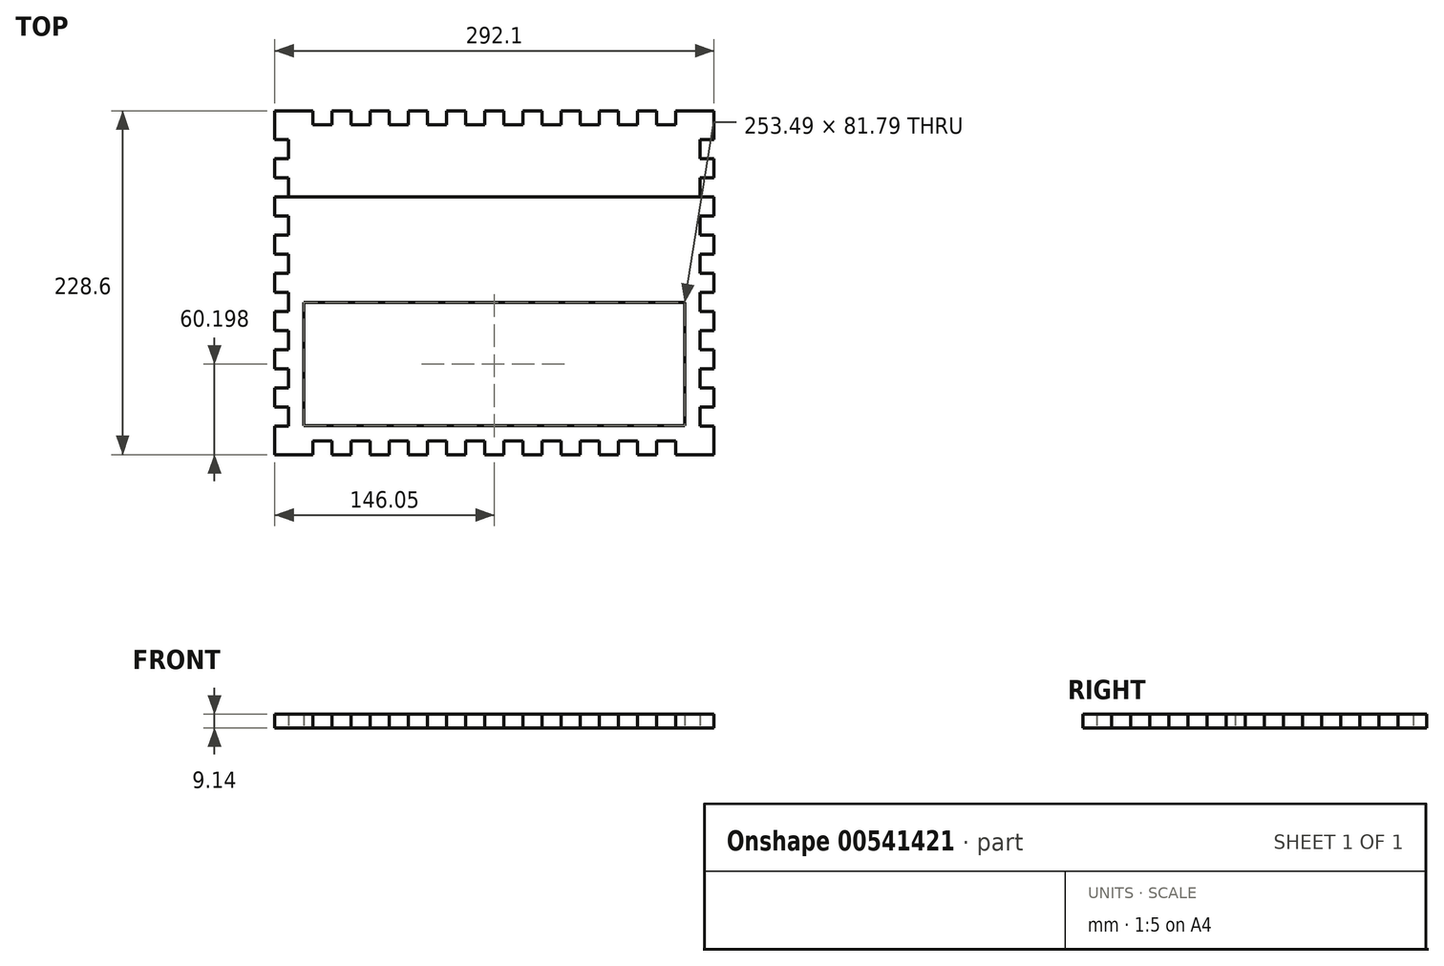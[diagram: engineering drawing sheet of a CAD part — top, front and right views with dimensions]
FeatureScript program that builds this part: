
annotation { "Feature Type Name" : "Feature", "Feature Type Description" : "" }
export const myFeature = defineFeature(function(context is Context, id is Id, definition is map)
    precondition{}
    {
        {
            var Q0;
            Q0=qCreatedBy(makeId("Top.planeOp"),FACE);
            var sketch = newSketch(context, id + "F0", { "sketchPlane" : qUnion([Q0])});
            skLineSegment(sketch, "E0.bottom", {"start": v(0, 0) * mm, "end": v(25.4, 0) * mm});
            skLineSegment(sketch, "E0.left", {"start": v(0, 0) * mm, "end": v(0, -19.05) * mm});
            skLineSegment(sketch, "E1", {"start": v(25.4, 0) * mm, "end": v(25.4, -9.14) * mm});
            skLineSegment(sketch, "E2", {"start": v(25.4, -9.14) * mm, "end": v(38.1, -9.14) * mm});
            skLineSegment(sketch, "E3", {"start": v(38.1, -9.14) * mm, "end": v(38.1, 0) * mm});
            skLineSegment(sketch, "E4", {"start": v(38.1, 0) * mm, "end": v(50.8, 0) * mm});
            skLineSegment(sketch, "E5", {"start": v(50.8, 0) * mm, "end": v(50.8, -9.14) * mm});
            skLineSegment(sketch, "E6", {"start": v(50.8, -9.14) * mm, "end": v(63.5, -9.14) * mm});
            skLineSegment(sketch, "E7", {"start": v(63.5, -9.14) * mm, "end": v(63.5, 0) * mm});
            skLineSegment(sketch, "E8", {"start": v(63.5, 0) * mm, "end": v(76.2, 0) * mm});
            skLineSegment(sketch, "E9", {"start": v(76.2, 0) * mm, "end": v(76.2, -9.14) * mm});
            skLineSegment(sketch, "E10", {"start": v(76.2, -9.14) * mm, "end": v(88.9, -9.14) * mm});
            skLineSegment(sketch, "E11", {"start": v(88.9, -9.14) * mm, "end": v(88.9, 0) * mm});
            skLineSegment(sketch, "E12", {"start": v(88.9, 0) * mm, "end": v(101.6, 0) * mm});
            skLineSegment(sketch, "E13", {"start": v(101.6, 0) * mm, "end": v(101.6, -9.14) * mm});
            skLineSegment(sketch, "E14", {"start": v(101.6, -9.14) * mm, "end": v(114.3, -9.14) * mm});
            skLineSegment(sketch, "E15", {"start": v(114.3, -9.14) * mm, "end": v(114.3, 0) * mm});
            skLineSegment(sketch, "E16", {"start": v(114.3, 0) * mm, "end": v(127, 0) * mm});
            skLineSegment(sketch, "E17", {"start": v(127, 0) * mm, "end": v(127, -9.14) * mm});
            skLineSegment(sketch, "E18", {"start": v(127, -9.14) * mm, "end": v(139.7, -9.14) * mm});
            skLineSegment(sketch, "E19", {"start": v(139.7, -9.14) * mm, "end": v(139.7, 0) * mm});
            skLineSegment(sketch, "E20.trimOffspring", {"start": v(139.7, 0) * mm, "end": v(152.4, 0) * mm});
            skLineSegment(sketch, "E21", {"start": v(152.4, 0) * mm, "end": v(152.4, -9.14) * mm});
            skLineSegment(sketch, "E22", {"start": v(152.4, -9.14) * mm, "end": v(165.1, -9.14) * mm});
            skLineSegment(sketch, "E23", {"start": v(165.1, -9.14) * mm, "end": v(165.1, 0) * mm});
            skLineSegment(sketch, "E24", {"start": v(165.1, 0) * mm, "end": v(177.8, 0) * mm});
            skLineSegment(sketch, "E25", {"start": v(177.8, 0) * mm, "end": v(177.8, -9.14) * mm});
            skLineSegment(sketch, "E26", {"start": v(177.8, -9.14) * mm, "end": v(190.5, -9.14) * mm});
            skLineSegment(sketch, "E27", {"start": v(190.5, -9.14) * mm, "end": v(190.5, 0) * mm});
            skLineSegment(sketch, "E28", {"start": v(190.5, 0) * mm, "end": v(203.2, 0) * mm});
            skLineSegment(sketch, "E29", {"start": v(203.2, 0) * mm, "end": v(203.2, -9.14) * mm});
            skLineSegment(sketch, "E30", {"start": v(203.2, -9.14) * mm, "end": v(215.9, -9.14) * mm});
            skLineSegment(sketch, "E31", {"start": v(215.9, -9.14) * mm, "end": v(215.9, 0) * mm});
            skLineSegment(sketch, "E32.trimOffspring", {"start": v(215.9, 0) * mm, "end": v(228.6, 0) * mm});
            skLineSegment(sketch, "E33", {"start": v(228.6, 0) * mm, "end": v(228.6, -9.14) * mm});
            skLineSegment(sketch, "E34", {"start": v(228.6, -9.14) * mm, "end": v(241.3, -9.14) * mm});
            skLineSegment(sketch, "E35", {"start": v(241.3, -9.14) * mm, "end": v(241.3, 0) * mm});
            skLineSegment(sketch, "E36", {"start": v(241.3, 0) * mm, "end": v(254, 0) * mm});
            skLineSegment(sketch, "E37", {"start": v(254, 0) * mm, "end": v(254, -9.14) * mm});
            skLineSegment(sketch, "E38", {"start": v(254, -9.14) * mm, "end": v(266.7, -9.14) * mm});
            skLineSegment(sketch, "E39", {"start": v(266.7, -9.14) * mm, "end": v(266.7, 0) * mm});
            skLineSegment(sketch, "E40.trimOffspring", {"start": v(266.7, 0) * mm, "end": v(292.1, 0) * mm});
            skLineSegment(sketch, "E41", {"start": v(0, -19.05) * mm, "end": v(9.14, -19.05) * mm});
            skLineSegment(sketch, "E42", {"start": v(9.14, -19.05) * mm, "end": v(9.14, -31.75) * mm});
            skLineSegment(sketch, "E43", {"start": v(9.14, -31.75) * mm, "end": v(0, -31.75) * mm});
            skLineSegment(sketch, "E44", {"start": v(0, -31.75) * mm, "end": v(0, -44.45) * mm});
            skLineSegment(sketch, "E45", {"start": v(0, -44.45) * mm, "end": v(9.14, -44.45) * mm});
            skLineSegment(sketch, "E46", {"start": v(9.14, -44.45) * mm, "end": v(9.14, -57.15) * mm});
            skLineSegment(sketch, "E47", {"start": v(9.14, -57.15) * mm, "end": v(0, -57.15) * mm});
            skLineSegment(sketch, "E48", {"start": v(0, -57.15) * mm, "end": v(0, -69.85) * mm});
            skLineSegment(sketch, "E49", {"start": v(0, -69.85) * mm, "end": v(9.14, -69.85) * mm});
            skLineSegment(sketch, "E50", {"start": v(9.14, -69.85) * mm, "end": v(9.14, -82.55) * mm});
            skLineSegment(sketch, "E51", {"start": v(9.14, -82.55) * mm, "end": v(0, -82.55) * mm});
            skLineSegment(sketch, "E52.trimOffspring", {"start": v(0, -82.55) * mm, "end": v(0, -95.25) * mm});
            skLineSegment(sketch, "E53", {"start": v(0, -95.25) * mm, "end": v(9.14, -95.25) * mm});
            skLineSegment(sketch, "E54", {"start": v(9.14, -95.25) * mm, "end": v(9.14, -107.95) * mm});
            skLineSegment(sketch, "E55", {"start": v(9.14, -107.95) * mm, "end": v(0, -107.95) * mm});
            skLineSegment(sketch, "E56", {"start": v(0, -107.95) * mm, "end": v(0, -120.65) * mm});
            skLineSegment(sketch, "E57", {"start": v(0, -120.65) * mm, "end": v(9.14, -120.65) * mm});
            skLineSegment(sketch, "E58", {"start": v(9.14, -120.65) * mm, "end": v(9.14, -133.35) * mm});
            skLineSegment(sketch, "E59", {"start": v(9.14, -133.35) * mm, "end": v(0, -133.35) * mm});
            skLineSegment(sketch, "E60", {"start": v(0, -133.35) * mm, "end": v(0, -146.05) * mm});
            skLineSegment(sketch, "E61", {"start": v(0, -146.05) * mm, "end": v(9.14, -146.05) * mm});
            skLineSegment(sketch, "E62", {"start": v(9.14, -146.05) * mm, "end": v(9.14, -158.75) * mm});
            skLineSegment(sketch, "E63", {"start": v(9.14, -158.75) * mm, "end": v(0, -158.75) * mm});
            skLineSegment(sketch, "E64.trimOffspring", {"start": v(0, -158.75) * mm, "end": v(0, -171.45) * mm});
            skLineSegment(sketch, "E65", {"start": v(0, -171.45) * mm, "end": v(9.14, -171.45) * mm});
            skLineSegment(sketch, "E66", {"start": v(9.14, -171.45) * mm, "end": v(9.14, -184.15) * mm});
            skLineSegment(sketch, "E67", {"start": v(9.14, -184.15) * mm, "end": v(0, -184.15) * mm});
            skLineSegment(sketch, "E68", {"start": v(0, -184.15) * mm, "end": v(0, -196.85) * mm});
            skLineSegment(sketch, "E69", {"start": v(0, -196.85) * mm, "end": v(9.14, -196.85) * mm});
            skLineSegment(sketch, "E70", {"start": v(9.14, -196.85) * mm, "end": v(9.14, -209.55) * mm});
            skLineSegment(sketch, "E71", {"start": v(9.14, -209.55) * mm, "end": v(0, -209.55) * mm});
            skLineSegment(sketch, "E72", {"start": v(0, -209.55) * mm, "end": v(0, -228.6) * mm});
            skLineSegment(sketch, "E73", {"start": v(146.05, 0) * mm, "end": v(146.05, -55.4) * mm, "construction": true});
            skLineSegment(sketch, "E74", {"start": v(0, -114.3) * mm, "end": v(76.06, -114.3) * mm, "construction": true});
            skLineSegment(sketch, "E75.MirrorCS", {"start": v(292.1, 0) * mm, "end": v(292.1, -19.05) * mm});
            skLineSegment(sketch, "E76.MirrorCS", {"start": v(292.1, -19.05) * mm, "end": v(282.96, -19.05) * mm});
            skLineSegment(sketch, "E77.MirrorCS", {"start": v(282.96, -19.05) * mm, "end": v(282.96, -31.75) * mm});
            skLineSegment(sketch, "E78.MirrorCS", {"start": v(282.96, -31.75) * mm, "end": v(292.1, -31.75) * mm});
            skLineSegment(sketch, "E79.MirrorCS", {"start": v(292.1, -31.75) * mm, "end": v(292.1, -44.45) * mm});
            skLineSegment(sketch, "E80.MirrorCS", {"start": v(292.1, -44.45) * mm, "end": v(282.96, -44.45) * mm});
            skLineSegment(sketch, "E81.MirrorCS", {"start": v(282.96, -44.45) * mm, "end": v(282.96, -57.15) * mm});
            skLineSegment(sketch, "E82.MirrorCS", {"start": v(282.96, -57.15) * mm, "end": v(292.1, -57.15) * mm});
            skLineSegment(sketch, "E83.MirrorCS", {"start": v(292.1, -57.15) * mm, "end": v(292.1, -69.85) * mm});
            skLineSegment(sketch, "E84.MirrorCS", {"start": v(292.1, -69.85) * mm, "end": v(282.96, -69.85) * mm});
            skLineSegment(sketch, "E85.MirrorCS", {"start": v(282.96, -69.85) * mm, "end": v(282.96, -82.55) * mm});
            skLineSegment(sketch, "E86.MirrorCS", {"start": v(282.96, -82.55) * mm, "end": v(292.1, -82.55) * mm});
            skLineSegment(sketch, "E87.MirrorCS", {"start": v(292.1, -82.55) * mm, "end": v(292.1, -95.25) * mm});
            skLineSegment(sketch, "E88.MirrorCS", {"start": v(292.1, -95.25) * mm, "end": v(282.96, -95.25) * mm});
            skLineSegment(sketch, "E89.MirrorCS", {"start": v(282.96, -95.25) * mm, "end": v(282.96, -107.95) * mm});
            skLineSegment(sketch, "E90.MirrorCS", {"start": v(282.96, -107.95) * mm, "end": v(292.1, -107.95) * mm});
            skLineSegment(sketch, "E91.MirrorCS", {"start": v(292.1, -107.95) * mm, "end": v(292.1, -120.65) * mm});
            skLineSegment(sketch, "E92.MirrorCS", {"start": v(292.1, -120.65) * mm, "end": v(282.96, -120.65) * mm});
            skLineSegment(sketch, "E93.MirrorCS", {"start": v(282.96, -120.65) * mm, "end": v(282.96, -133.35) * mm});
            skLineSegment(sketch, "E94.MirrorCS", {"start": v(282.96, -133.35) * mm, "end": v(292.1, -133.35) * mm});
            skLineSegment(sketch, "E95.MirrorCS", {"start": v(292.1, -133.35) * mm, "end": v(292.1, -146.05) * mm});
            skLineSegment(sketch, "E96.MirrorCS", {"start": v(292.1, -146.05) * mm, "end": v(282.96, -146.05) * mm});
            skLineSegment(sketch, "E97.MirrorCS", {"start": v(282.96, -146.05) * mm, "end": v(282.96, -158.75) * mm});
            skLineSegment(sketch, "E98.MirrorCS", {"start": v(282.96, -158.75) * mm, "end": v(292.1, -158.75) * mm});
            skLineSegment(sketch, "E99.MirrorCS", {"start": v(292.1, -158.75) * mm, "end": v(292.1, -171.45) * mm});
            skLineSegment(sketch, "E100.MirrorCS", {"start": v(292.1, -171.45) * mm, "end": v(282.96, -171.45) * mm});
            skLineSegment(sketch, "E101.MirrorCS", {"start": v(282.96, -171.45) * mm, "end": v(282.96, -184.15) * mm});
            skLineSegment(sketch, "E102.MirrorCS", {"start": v(282.96, -184.15) * mm, "end": v(292.1, -184.15) * mm});
            skLineSegment(sketch, "E103.MirrorCS", {"start": v(292.1, -184.15) * mm, "end": v(292.1, -196.85) * mm});
            skLineSegment(sketch, "E104.MirrorCS", {"start": v(292.1, -196.85) * mm, "end": v(282.96, -196.85) * mm});
            skLineSegment(sketch, "E105.MirrorCS", {"start": v(282.96, -196.85) * mm, "end": v(282.96, -209.55) * mm});
            skLineSegment(sketch, "E106.MirrorCS", {"start": v(282.96, -209.55) * mm, "end": v(292.1, -209.55) * mm});
            skLineSegment(sketch, "E107.MirrorCS", {"start": v(292.1, -209.55) * mm, "end": v(292.1, -228.6) * mm});
            skLineSegment(sketch, "E108.MirrorCS", {"start": v(0, -228.6) * mm, "end": v(25.4, -228.6) * mm});
            skLineSegment(sketch, "E109.MirrorCS", {"start": v(25.4, -228.6) * mm, "end": v(25.4, -219.46) * mm});
            skLineSegment(sketch, "E110.MirrorCS", {"start": v(25.4, -219.46) * mm, "end": v(38.1, -219.46) * mm});
            skLineSegment(sketch, "E111.MirrorCS", {"start": v(38.1, -219.46) * mm, "end": v(38.1, -228.6) * mm});
            skLineSegment(sketch, "E112.MirrorCS", {"start": v(38.1, -228.6) * mm, "end": v(50.8, -228.6) * mm});
            skLineSegment(sketch, "E113.MirrorCS", {"start": v(50.8, -228.6) * mm, "end": v(50.8, -219.46) * mm});
            skLineSegment(sketch, "E114.MirrorCS", {"start": v(50.8, -219.46) * mm, "end": v(63.5, -219.46) * mm});
            skLineSegment(sketch, "E115.MirrorCS", {"start": v(63.5, -219.46) * mm, "end": v(63.5, -228.6) * mm});
            skLineSegment(sketch, "E116.MirrorCS", {"start": v(63.5, -228.6) * mm, "end": v(76.2, -228.6) * mm});
            skLineSegment(sketch, "E117.MirrorCS", {"start": v(76.2, -228.6) * mm, "end": v(76.2, -219.46) * mm});
            skLineSegment(sketch, "E118.MirrorCS", {"start": v(76.2, -219.46) * mm, "end": v(88.9, -219.46) * mm});
            skLineSegment(sketch, "E119.MirrorCS", {"start": v(88.9, -219.46) * mm, "end": v(88.9, -228.6) * mm});
            skLineSegment(sketch, "E120.MirrorCS", {"start": v(88.9, -228.6) * mm, "end": v(101.6, -228.6) * mm});
            skLineSegment(sketch, "E121.MirrorCS", {"start": v(101.6, -228.6) * mm, "end": v(101.6, -219.46) * mm});
            skLineSegment(sketch, "E122.MirrorCS", {"start": v(101.6, -219.46) * mm, "end": v(114.3, -219.46) * mm});
            skLineSegment(sketch, "E123.MirrorCS", {"start": v(114.3, -219.46) * mm, "end": v(114.3, -228.6) * mm});
            skLineSegment(sketch, "E124.MirrorCS", {"start": v(114.3, -228.6) * mm, "end": v(127, -228.6) * mm});
            skLineSegment(sketch, "E125.MirrorCS", {"start": v(127, -228.6) * mm, "end": v(127, -219.46) * mm});
            skLineSegment(sketch, "E126.MirrorCS", {"start": v(127, -219.46) * mm, "end": v(139.7, -219.46) * mm});
            skLineSegment(sketch, "E127.MirrorCS", {"start": v(139.7, -219.46) * mm, "end": v(139.7, -228.6) * mm});
            skLineSegment(sketch, "E128.MirrorCS", {"start": v(139.7, -228.6) * mm, "end": v(152.4, -228.6) * mm});
            skLineSegment(sketch, "E129.MirrorCS", {"start": v(152.4, -228.6) * mm, "end": v(152.4, -219.46) * mm});
            skLineSegment(sketch, "E130.MirrorCS", {"start": v(152.4, -219.46) * mm, "end": v(165.1, -219.46) * mm});
            skLineSegment(sketch, "E131.MirrorCS", {"start": v(165.1, -219.46) * mm, "end": v(165.1, -228.6) * mm});
            skLineSegment(sketch, "E132.MirrorCS", {"start": v(165.1, -228.6) * mm, "end": v(177.8, -228.6) * mm});
            skLineSegment(sketch, "E133.MirrorCS", {"start": v(177.8, -228.6) * mm, "end": v(177.8, -219.46) * mm});
            skLineSegment(sketch, "E134.MirrorCS", {"start": v(177.8, -219.46) * mm, "end": v(190.5, -219.46) * mm});
            skLineSegment(sketch, "E135.MirrorCS", {"start": v(190.5, -219.46) * mm, "end": v(190.5, -228.6) * mm});
            skLineSegment(sketch, "E136.MirrorCS", {"start": v(190.5, -228.6) * mm, "end": v(203.2, -228.6) * mm});
            skLineSegment(sketch, "E137.MirrorCS", {"start": v(203.2, -228.6) * mm, "end": v(203.2, -219.46) * mm});
            skLineSegment(sketch, "E138.MirrorCS", {"start": v(203.2, -219.46) * mm, "end": v(215.9, -219.46) * mm});
            skLineSegment(sketch, "E139.MirrorCS", {"start": v(215.9, -219.46) * mm, "end": v(215.9, -228.6) * mm});
            skLineSegment(sketch, "E140.MirrorCS", {"start": v(215.9, -228.6) * mm, "end": v(228.6, -228.6) * mm});
            skLineSegment(sketch, "E141.MirrorCS", {"start": v(228.6, -228.6) * mm, "end": v(228.6, -219.46) * mm});
            skLineSegment(sketch, "E142.MirrorCS", {"start": v(228.6, -219.46) * mm, "end": v(241.3, -219.46) * mm});
            skLineSegment(sketch, "E143.MirrorCS", {"start": v(241.3, -219.46) * mm, "end": v(241.3, -228.6) * mm});
            skLineSegment(sketch, "E144.MirrorCS", {"start": v(241.3, -228.6) * mm, "end": v(254, -228.6) * mm});
            skLineSegment(sketch, "E145.MirrorCS", {"start": v(254, -228.6) * mm, "end": v(254, -219.46) * mm});
            skLineSegment(sketch, "E146.MirrorCS", {"start": v(254, -219.46) * mm, "end": v(266.7, -219.46) * mm});
            skLineSegment(sketch, "E147.MirrorCS", {"start": v(266.7, -219.46) * mm, "end": v(266.7, -228.6) * mm});
            skLineSegment(sketch, "E148.MirrorCS", {"start": v(266.7, -228.6) * mm, "end": v(292.1, -228.6) * mm});
            skLineSegment(sketch, "E149", {"start": v(9.14, -57.15) * mm, "end": v(282.96, -57.15) * mm});
            skLineSegment(sketch, "E150.bottom", {"start": v(19.3, -127.5) * mm, "end": v(272.8, -127.5) * mm});
            skLineSegment(sketch, "E150.top", {"start": v(19.3, -209.3) * mm, "end": v(272.8, -209.3) * mm});
            skLineSegment(sketch, "E150.left", {"start": v(19.3, -127.5) * mm, "end": v(19.3, -209.3) * mm});
            skLineSegment(sketch, "E150.right", {"start": v(272.8, -127.5) * mm, "end": v(272.8, -209.3) * mm});
            skSolve(sketch);
        }
        {
            var Q0;
            Q0=makeQuery(id+"F0.imprint","IMPRINT",FACE,{"disambiguationData":[TD([[makeQuery(id+"F0.imprint","IMPRINT",EDGE,{"derivedFrom":sQuery(id+"F0.wireOp",EDGE,"E0.bottom")}),-1.0]])]});
            extrude(context, id + "F1", {"entities" : qUnion([Q0]), "depth" : 9.14 * mm, "offsetDistance" : 25.4 * mm});
        }
        {
            var Q0;
            Q0=makeQuery(id+"F0.imprint","IMPRINT",FACE,{"disambiguationData":[TD([[makeQuery(id+"F0.imprint","IMPRINT",EDGE,{"derivedFrom":sQuery(id+"F0.wireOp",EDGE,"E47")}),1.0]])]});
            extrude(context, id + "F2", {"entities" : qUnion([Q0]), "depth" : 9.14 * mm, "offsetDistance" : 25.4 * mm});
        }
    });
